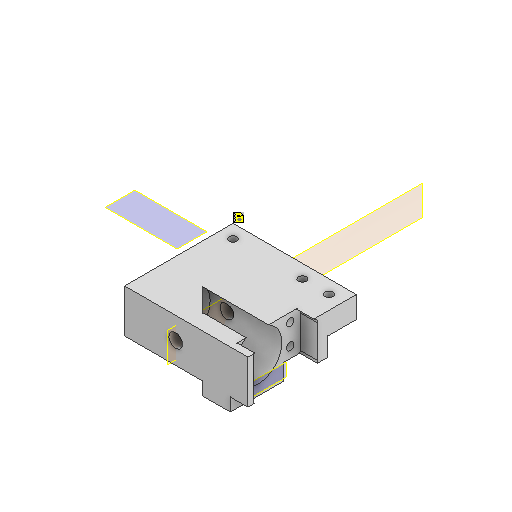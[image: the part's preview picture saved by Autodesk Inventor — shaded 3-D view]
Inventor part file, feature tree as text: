
AUTODESK INVENTOR PART (.ipt)
format: ipt  version: 2025.3 (Build 293356000, 356)  size: 376,832 bytes
history: native  units: mm
features: reference x21, extrude x14, sketch x11, plane x10, projected_geometry x7, other x7
ambient origin geometry x8: Origin, YZ Plane, XZ Plane, XY Plane, X Axis, Y Axis, Z Axis, Center Point
bodies: Body1 (feature_tree)
feature tree (70):
  plane  "Arbeitsebene6"
  extrude  "Extrusion12"  Depth=0.5mm
  extrude  "Extrusion13"  Depth=12.5mm TaperAngle=0.0deg
  plane  "Arbeitsebene7"
  extrude  "Extrusion15"  Depth=35.97mm TaperAngle=0.0deg
  plane  "Arbeitsebene8"
  plane  "Arbeitsebene9"
  plane  "Arbeitsebene10"
  sketch  "Skizze21"  dims[d75=18.0mm d76=35.97mm d77=0.0mm]
  plane  "Arbeitsebene11"
  extrude  "Extrusion18"  TaperAngle=45.0deg  [1 undecoded]
  extrude  "Extrusion19"  Depth=14.0mm TaperAngle=0.0deg
  extrude  "Extrusion20"  Depth=0.5mm
  plane  "Arbeitsebene12"
  extrude  "Extrusion22"  TaperAngle=0.0deg  [1 undecoded]
  extrude  "Extrusion23"  Depth=0.5mm
  extrude  "Extrusion27"  TaperAngle=0.0deg  [1 undecoded]
  sketch  "Skizze31"  dims[d93=20.0mm d94=0.5mm]
  plane  "Arbeitsebene13"
  extrude  "Extrusion28"  Depth=10.0mm
  extrude  "Extrusion29"  Depth=10.0mm TaperAngle=0.0deg
  sketch  "Skizze33"  dims[d107=12.0mm d108=0.0mm d109=0.0mm d110=0.0mm]
  plane  "Arbeitsebene14"
  extrude  "Extrusion30"  Depth=10.0mm TaperAngle=0.0deg
  extrude  "Extrusion31"  Depth=10.0mm
  sketch  "Skizze35"  dims[d114=0.1mm d116=10.0mm d117=0.0mm d118=10.0mm d119=0.0mm d120=6.0mm d121=9.5mm d122=9.5mm d123=2.0mm d124=2.0mm d125=2.0mm d126=2.5mm d127=10.0mm d128=0.0mm d15=0.5mm d16=0.872665mm d17=0.5mm d18=0.872665mm]
  plane  "Arbeitsebene15"
  extrude  "Extrusion32"  Depth=10.0mm
  sketch  "Skizze13"  dims[d58=8.0mm d59=0.0mm d60=0.5mm]
  reference  "Referenz11"
  reference  "Referenz12"
  reference  "Referenz13"
  reference  "Referenz14"
  sketch  "Skizze16"  dims[d62=8.0mm d63=0.0mm d66=12.5mm d67=0.0mm]
  projected_geometry  "Projizierte Kontur9"
  reference  "Referenz15"
  reference  "Referenz17"
  reference  "Referenz18"
  reference  "Referenz19"
  reference  "Referenz20"
  reference  "Referenz21"
  reference  "Referenz22"
  reference  "Referenz25"
  sketch  "Skizze22"  dims[d78=21.0mm d79=45.0deg]
  projected_geometry  "Projizierte Kontur10"
  sketch  "Skizze23"  dims[d80=1.2mm d81=14.0mm d82=0.0mm]
  projected_geometry  "Projizierte Kontur11"
  reference  "Referenz26"
  reference  "Referenz27"
  sketch  "Skizze26"  dims[d83=14.0mm d84=0.0mm d87=0.5mm]
  projected_geometry  "Projizierte Kontur13"
  sketch  "Skizze30"  dims[d88=10.0mm d89=0.0mm d90=0.0mm d91=0.0mm]
  reference  "Referenz30"
  reference  "Referenz31"
  reference  "Referenz32"
  reference  "Referenz33"
  reference  "Referenz34"
  reference  "Referenz35"
  reference  "Referenz36"
  sketch  "Skizze34"  dims[d111=10.0mm d112=0.0mm d113=0.1mm]
  projected_geometry  "Projizierte Kontur15"
  projected_geometry  "Projizierte Kontur16"
  projected_geometry  "Projizierte Kontur17"
  other  "Assemlby_lightsheet_generator_passive_v2.iam"
  other  "30_Scanlens_Laseradaper_lid_v1:1"
  other  "<userpath>\Documents\HoLiSheet\INVENTOR\Assemlby_lightsheet_generator_passive_v2.iam"
  other  "30_Lightsheet_generator_passive_lid_v1:1"
  other  "00_Thorlabs_LJ1878L1-A-Step:1"
  other  "00_SMAConnector_fiber copy:1"
  other  "30_Laser_to_M12Adapter:1"
note: 3 required parameter values undecoded (feature->parameter linkage not recoverable at this tier; creation-order binding heuristic only, values carry confidence <= 0.55)
